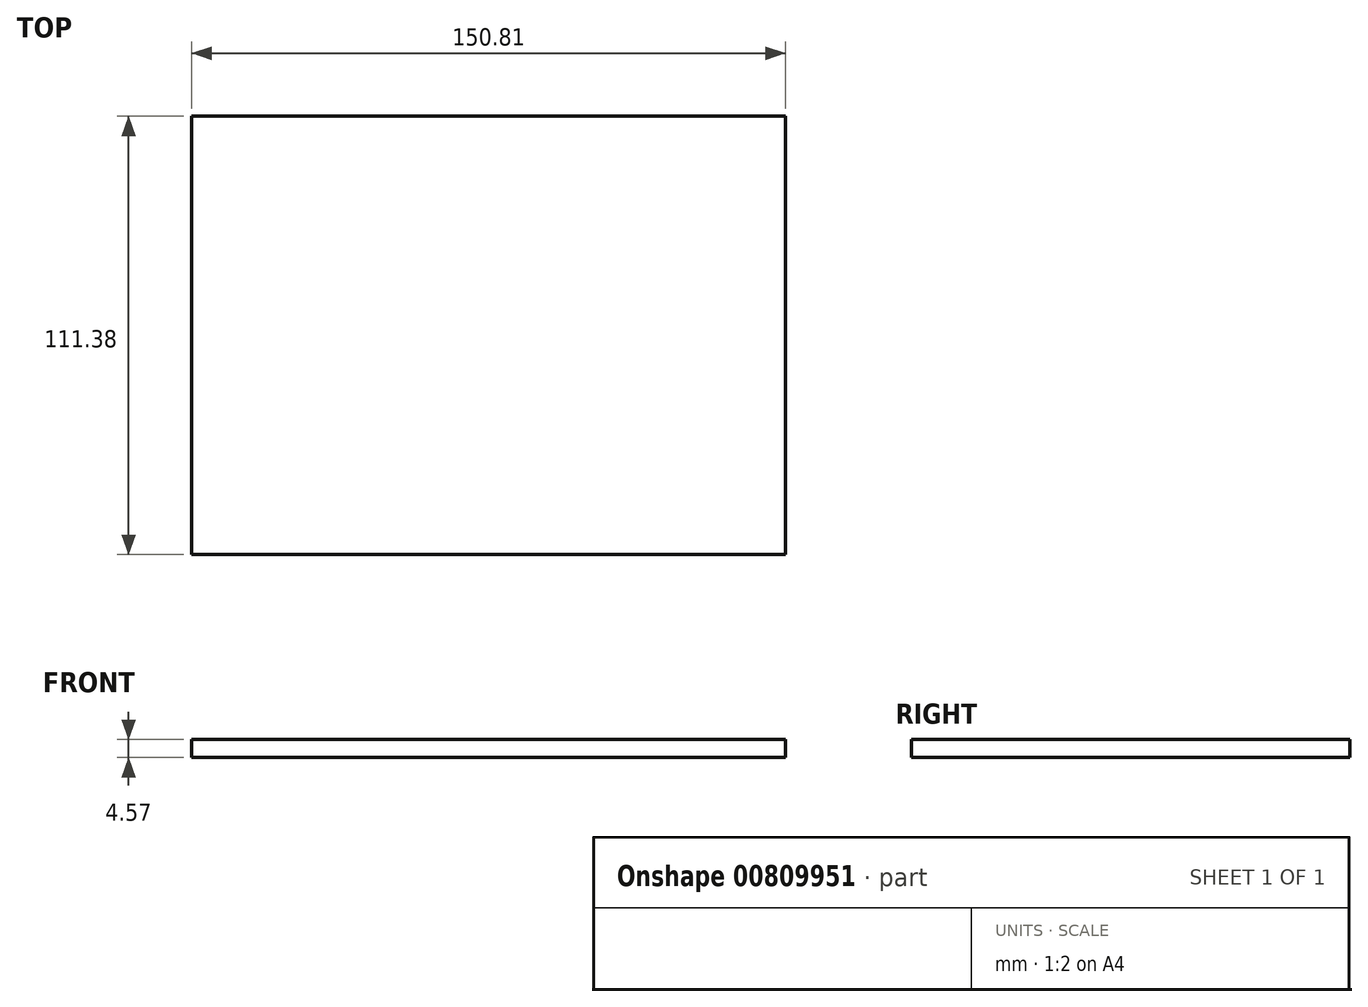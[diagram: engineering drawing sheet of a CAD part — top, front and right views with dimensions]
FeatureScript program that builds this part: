
annotation { "Feature Type Name" : "Feature", "Feature Type Description" : "" }
export const myFeature = defineFeature(function(context is Context, id is Id, definition is map)
    precondition{}
    {
        {
            var Q0;
            Q0=qCreatedBy(makeId("Top.planeOp"),FACE);
            var sketch = newSketch(context, id + "F0", { "sketchPlane" : qUnion([Q0])});
            skLineSegment(sketch, "E0.bottom", {"start": v(-74.97, 55.98) * mm, "end": v(75.84, 55.98) * mm});
            skLineSegment(sketch, "E0.top", {"start": v(-74.97, -55.4) * mm, "end": v(75.84, -55.4) * mm});
            skLineSegment(sketch, "E0.left", {"start": v(-74.97, 55.98) * mm, "end": v(-74.97, -55.4) * mm});
            skLineSegment(sketch, "E0.right", {"start": v(75.84, 55.98) * mm, "end": v(75.84, -55.4) * mm});
            skSolve(sketch);
        }
        {
            var Q0;
            Q0 = qSketchRegion(id + "F0", true);
            extrude(context, id + "F1", {"entities" : qUnion([Q0]), "depth" : 4.57 * mm, "offsetDistance" : 25.4 * mm});
        }
    });
